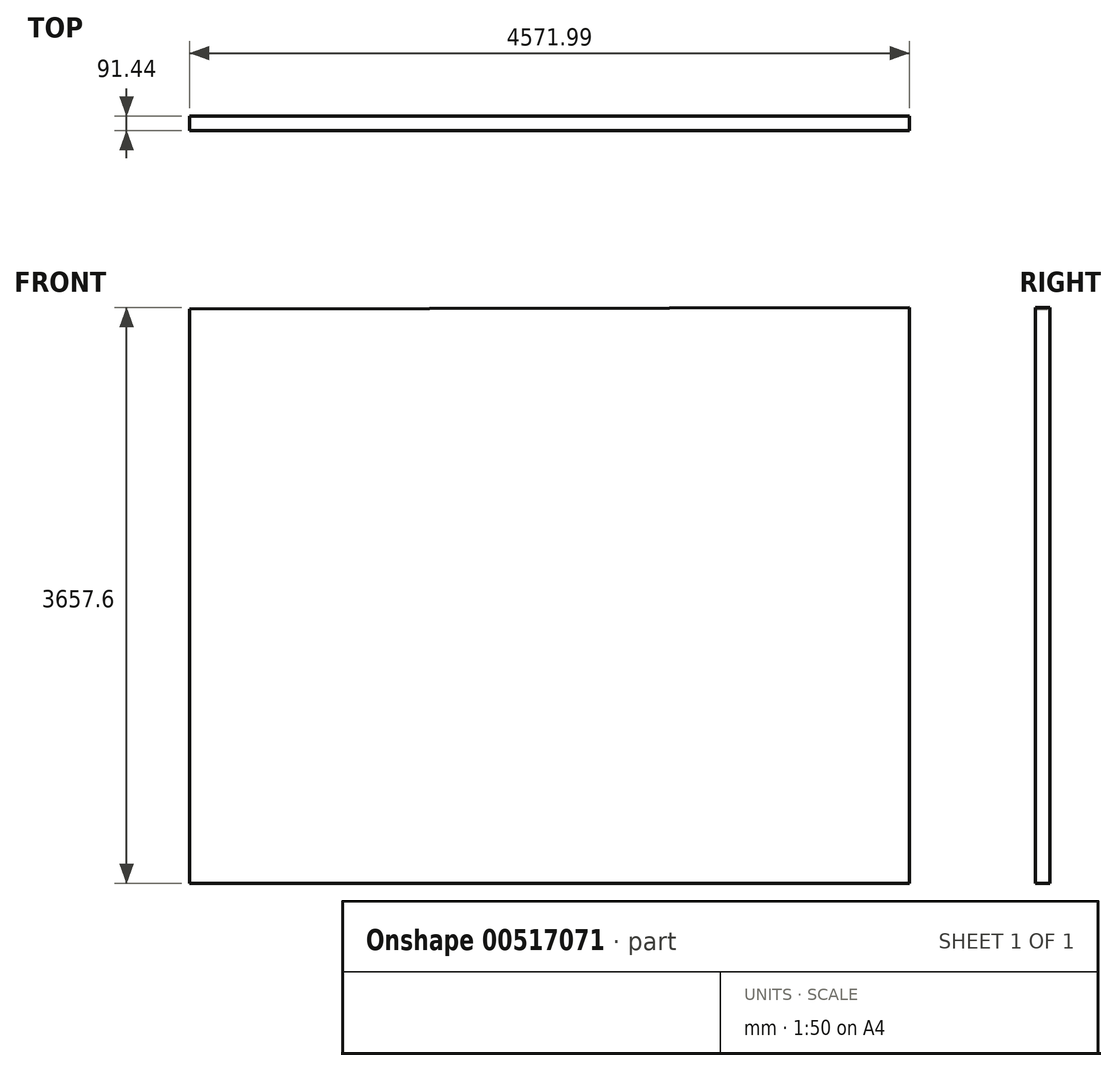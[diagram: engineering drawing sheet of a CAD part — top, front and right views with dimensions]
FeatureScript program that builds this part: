
annotation { "Feature Type Name" : "Feature", "Feature Type Description" : "" }
export const myFeature = defineFeature(function(context is Context, id is Id, definition is map)
    precondition{}
    {
        {
            var Q0;
            Q0=qCreatedBy(makeId("Front.planeOp"),FACE);
            var sketch = newSketch(context, id + "F0", { "sketchPlane" : qUnion([Q0])});
            skLineSegment(sketch, "E0", {"start": v(-2692.26, 1822) * mm, "end": v(-2692.26, -1824.82) * mm});
            skLineSegment(sketch, "E1", {"start": v(-2692.26, -1824.82) * mm, "end": v(1879.73, -1824.82) * mm});
            skLineSegment(sketch, "E2", {"start": v(1879.73, -1824.82) * mm, "end": v(1879.73, 1832.78) * mm});
            skLineSegment(sketch, "E3", {"start": v(1879.73, 1832.78) * mm, "end": v(-2692.26, 1822) * mm});
            skSolve(sketch);
        }
        {
            var Q0;
            Q0=makeQuery(id+"F0.imprint","IMPRINT",FACE,{"disambiguationData":[TD([[makeQuery(id+"F0.imprint","IMPRINT",EDGE,{"derivedFrom":sQuery(id+"F0.wireOp",EDGE,"E0")}),1.0]])]});
            extrude(context, id + "F1", {"entities" : qUnion([Q0]), "depth" : 91.44 * mm, "offsetDistance" : 30.48 * mm});
        }
    });
